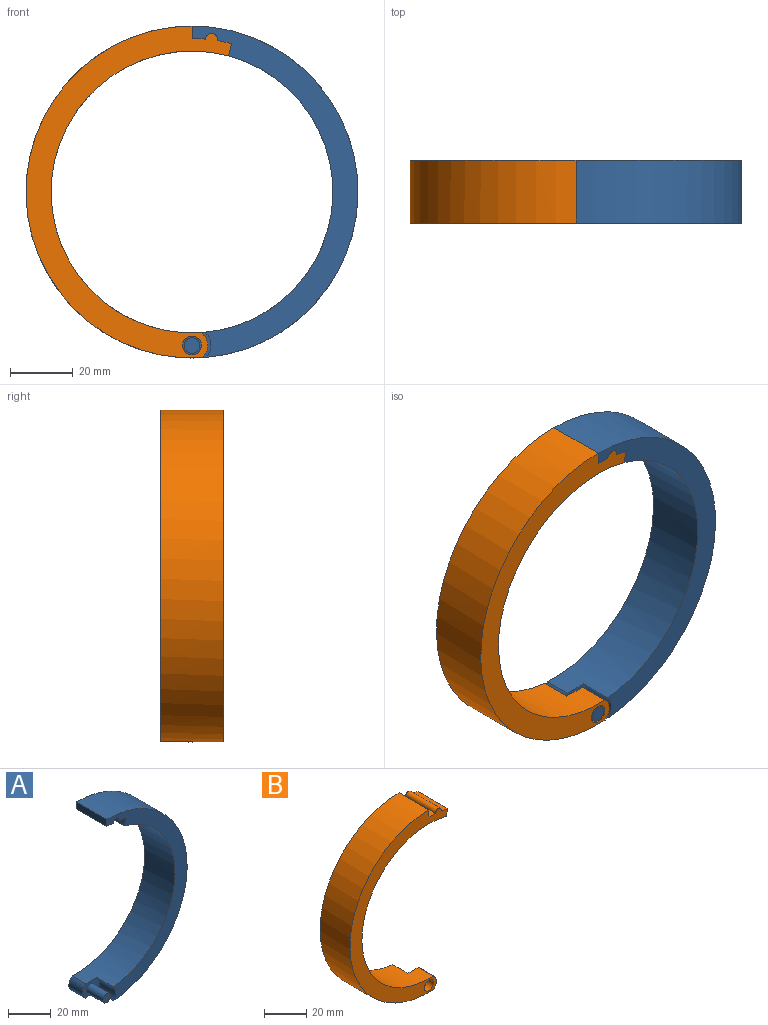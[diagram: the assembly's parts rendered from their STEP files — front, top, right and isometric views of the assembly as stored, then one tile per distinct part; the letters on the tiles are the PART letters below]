
ASSEMBLY  parts=2 mates=1
PART A: 14 faces, bbox 58x20x106 mm
  f0: cylinder r=49mm len=20mm, axis (0,1,0), area 90.4mm2, adj f1,f7,f8,f9
  f1: plane 20x3.86mm, normal (-0.97,0,0.26), area 80mm2, adj f0,f2,f8,f9
  f2: cylinder r=45mm len=88.47mm, axis (0,1,0), area 2570.5mm2, adj f1,f3,f8,f9,f10,f11
  f3: cylinder r=6mm len=11mm, axis (0,1,0), area 96.4mm2, adj f2,f4,f8,f11
  f4: cylinder r=53mm len=106mm, axis (0,1,0), area 3307mm2, adj f3,f5,f8,f9,f10,f11
  f5: plane 20x4mm, normal (-1,0,0), area 80mm2, adj f4,f6,f8,f9
  f6: cylinder r=49mm len=20mm, axis (0,1,0), area 86.2mm2, adj f5,f7,f8,f9
  f7: cylinder r=2mm len=20mm, axis (0,1,0), area 127.3mm2, adj f0,f6,f8,f9
  f8: plane 105.8x53mm, normal (0,-1,0), area 1131.8mm2, adj f0,f1,f2,f3,f4,f5,f6,f7
  f9: plane 106x58mm, normal (0,1,0), area 1211.1mm2, adj f0,f1,f2,f4,f5,f6,f7,f10
  f10: cylinder r=5mm len=9mm, axis (0,1,0), area 83.5mm2, adj f2,f4,f9,f11
  f11: plane 11x8.2mm, normal (0,-1,0), area 59.7mm2, adj f2,f3,f4,f10,f13
  f12: plane 5x5mm, normal (0,-1,0), area 19.6mm2, adj f13
  f13: cylinder r=2.5mm len=11mm, axis (0,1,0), area 172.8mm2, adj f11,f12
PART B: 13 faces, bbox 65.7x20x106 mm
  f0: cylinder r=45mm len=90mm, axis (0,1,0), area 3048.9mm2, adj f1,f7,f9,f10,f11,f12
  f1: plane 20x3.86mm, normal (0.97,0,-0.26), area 80mm2, adj f0,f2,f9,f10
  f2: cylinder r=49mm len=20mm, axis (0,1,0), area 90.4mm2, adj f1,f3,f9,f10
  f3: cylinder r=2mm len=20mm, axis (0,1,0), area 127.3mm2, adj f2,f4,f9,f10
  f4: cylinder r=49mm len=20mm, axis (0,1,0), area 86.2mm2, adj f3,f5,f9,f10
  f5: plane 20x4mm, normal (1,0,0), area 80mm2, adj f4,f6,f9,f10
  f6: cylinder r=53mm len=106mm, axis (0,1,0), area 3314.8mm2, adj f5,f7,f9,f10,f11,f12
  f7: cylinder r=5mm len=10mm, axis (0,1,0), area 92.8mm2, adj f0,f6,f9,f12
  f8: cylinder r=3mm len=10mm, axis (0,1,0), area 188.5mm2, adj f9,f12
  f9: plane 106x65.68mm, normal (0,-1,0), area 1294mm2, adj f0,f1,f2,f3,f4,f5,f6,f7
  f10: plane 105.8x65.68mm, normal (0,1,0), area 1242.9mm2, adj f0,f1,f2,f3,f4,f5,f6,f11
  f11: cylinder r=6mm len=10mm, axis (0,1,0), area 87.7mm2, adj f0,f6,f10,f12
  f12: plane 11x8.2mm, normal (0,1,0), area 51.1mm2, adj f0,f6,f7,f8,f11
PLACE A at identity
PLACE B at identity
MATE revolute A.f13 <-> B.f8  axis (0,-1,0) through (0,-20,-49)mm
